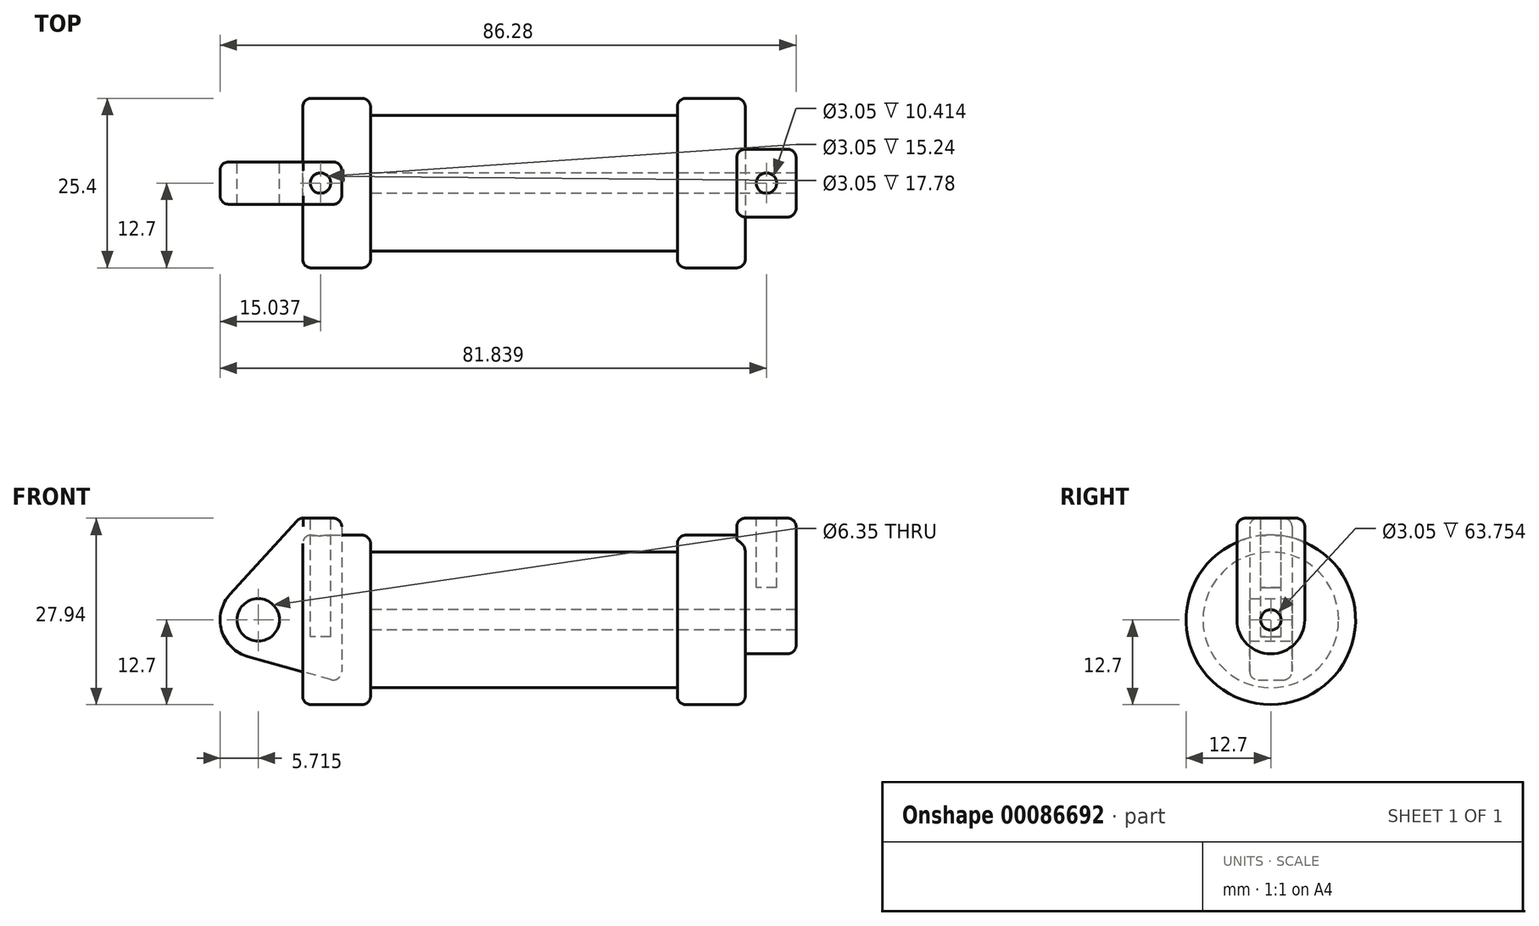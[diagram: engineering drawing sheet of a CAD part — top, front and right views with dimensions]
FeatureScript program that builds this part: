
annotation { "Feature Type Name" : "Feature", "Feature Type Description" : "" }
export const myFeature = defineFeature(function(context is Context, id is Id, definition is map)
    precondition{}
    {
        {
            var Q0;
            Q0=qCreatedBy(makeId("Front.planeOp"),FACE);
            var sketch = newSketch(context, id + "F0", { "sketchPlane" : qUnion([Q0])});
            skLineSegment(sketch, "E0", {"start": v(0, 0) * mm, "end": v(0, 12.7) * mm});
            skLineSegment(sketch, "E1", {"start": v(0, 12.7) * mm, "end": v(10.16, 12.7) * mm});
            skLineSegment(sketch, "E2", {"start": v(10.16, 12.7) * mm, "end": v(10.16, 10.16) * mm});
            skLineSegment(sketch, "E3", {"start": v(10.16, 10.16) * mm, "end": v(56.13, 10.16) * mm});
            skLineSegment(sketch, "E4", {"start": v(56.13, 10.16) * mm, "end": v(56.13, 12.7) * mm});
            skLineSegment(sketch, "E5", {"start": v(56.13, 12.7) * mm, "end": v(66.3, 12.7) * mm});
            skLineSegment(sketch, "E6", {"start": v(66.3, 12.7) * mm, "end": v(66.3, 0) * mm});
            skLineSegment(sketch, "E7", {"start": v(66.3, 0) * mm, "end": v(0, 0) * mm});
            skLineSegment(sketch, "E8", {"start": v(5.84, 15.24) * mm, "end": v(-0.5, 15.24) * mm});
            skLineSegment(sketch, "E9", {"start": v(-0.5, 15.24) * mm, "end": v(-10.88, 3.85) * mm});
            skLineSegment(sketch, "E10", {"start": v(0, 0) * mm, "end": v(-6.65, 0) * mm});
            skCircle(sketch, "E11", {"center": v(-6.65, 0) * mm, "radius": 5.72 * mm});
            skCircle(sketch, "E12", {"center": v(-6.65, 0) * mm, "radius": 3.18 * mm});
            skLineSegment(sketch, "E13", {"start": v(5.84, 15.24) * mm, "end": v(5.84, -9.4) * mm});
            skLineSegment(sketch, "E14", {"start": v(5.84, -9.4) * mm, "end": v(-8.18, -5.5) * mm});
            skSolve(sketch);
        }
        {
            var Q0;
            {var subQ3=sQuery(id+"F0.wireOp",EDGE,"E0");Q0=makeQuery(id+"F0.imprint","IMPRINT",FACE,{"disambiguationData":[TD([[makeQuery(id+"F0.imprint","IMPRINT",EDGE,{"derivedFrom":subQ3}),1.0]])]});}
            var Q1;
            {var subQ4=sQuery(id+"F0.wireOp",EDGE,"E12");Q1=makeQuery(id+"F0.imprint","IMPRINT",FACE,{"disambiguationData":[TD([[makeQuery(id+"F0.imprint","IMPRINT",EDGE,{"derivedFrom":subQ4}),-1.0]])]});}
            var Q2;
            {var subQ0=sQuery(id+"F0.wireOp",EDGE,"E14");Q2=makeQuery(id+"F0.imprint","IMPRINT",FACE,{"disambiguationData":[TD([[makeQuery(id+"F0.imprint","IMPRINT",EDGE,{"derivedFrom":subQ0}),-1.0]])]});}
            var Q3;
            {var subQ0=sQuery(id+"F0.wireOp",EDGE,"E0");Q3=makeQuery(id+"F0.imprint","IMPRINT",FACE,{"disambiguationData":[TD([[makeQuery(id+"F0.imprint","IMPRINT",EDGE,{"derivedFrom":subQ0}),-1.0]])]});}
            extrude(context, id + "F1", {"entities" : qUnion([Q0, Q1, Q2, Q3]), "endBound" : BoundingType.SYMMETRIC, "depth" : 6.35 * mm});
        }
        {
            var Q0;
            {var subQ0=sQuery(id+"F0.wireOp",EDGE,"E2");Q0=makeQuery(id+"F0.imprint","IMPRINT",FACE,{"disambiguationData":[TD([[makeQuery(id+"F0.imprint","IMPRINT",EDGE,{"derivedFrom":subQ0}),-1.0]])]});}
            var Q1;
            {var subQ0=sQuery(id+"F0.wireOp",EDGE,"E0");Q1=makeQuery(id+"F0.imprint","IMPRINT",FACE,{"disambiguationData":[TD([[makeQuery(id+"F0.imprint","IMPRINT",EDGE,{"derivedFrom":subQ0}),-1.0]])]});}
            var Q2;
            Q2=sQuery(id+"F0.wireOp",EDGE,"E7");
            revolve(context, id + "F2", {"entities" : qUnion([Q0, Q1]), "axis" : qUnion([Q2]), "revolveType" : RevolveType.FULL});
        }
        {
            var Q0;
            Q0=makeQuery(id+"F2.opRevolve","SWEPT_FACE",FACE,{"disambiguationData":[OSD([sQuery(id+"F0.wireOp",EDGE,"E6")])]});
            var sketch = newSketch(context, id + "F3", { "sketchPlane" : qUnion([Q0])});
            skCircle(sketch, "E15", {"center": v(0, 0) * mm, "radius": 1.52 * mm});
            skCircle(sketch, "E16", {"center": v(0, 0) * mm, "radius": 5.08 * mm});
            skLineSegment(sketch, "E17", {"start": v(-5.08, 0) * mm, "end": v(-5.08, 15.24) * mm});
            skLineSegment(sketch, "E18", {"start": v(-5.08, 15.24) * mm, "end": v(5.08, 15.24) * mm});
            skLineSegment(sketch, "E19", {"start": v(5.08, 15.24) * mm, "end": v(5.08, 0) * mm});
            skSolve(sketch);
        }
        {
            var Q0;
            {var subQ0=sQuery(id+"F3.wireOp",EDGE,"E18");Q0=makeQuery(id+"F3.imprint","IMPRINT",FACE,{"disambiguationData":[TD([[makeQuery(id+"F3.imprint","IMPRINT",EDGE,{"derivedFrom":subQ0}),-1.0]])]});}
            var Q1;
            {var subQ0=sQuery(id+"F3.wireOp",EDGE,"E17");var subQ1=sQuery(id+"F3.wireOp",EDGE,"E16");var subQ2=makeQuery(id+"F3.imprint","INTERSECT",VERTEX,{"derivedFrom":[subQ1,subQ0]});Q1=makeQuery(id+"F3.imprint","IMPRINT",FACE,{"disambiguationData":[TD([[makeQuery(id+"F3.imprint","IMPRINT",EDGE,{"disambiguationData":[TD([[subQ2,1.0]])],"derivedFrom":subQ1}),-1.0]])]});}
            var Q2;
            Q2=makeQuery(id+"F3.imprint","IMPRINT",FACE,{"disambiguationData":[TD([[makeQuery(id+"F3.imprint","IMPRINT",EDGE,{"derivedFrom":sQuery(id+"F3.wireOp",EDGE,"E15")}),-1.0]])]});
            extrude(context, id + "F4", {"entities" : qUnion([Q0, Q1, Q2]), "operationType" : NewBodyOperationType.ADD, "depth" : 7.62 * mm});
        }
        {
            var Q0;
            {var subQ0=sQuery(id+"F3.wireOp",EDGE,"E18");Q0=makeQuery(id+"F3.imprint","IMPRINT",FACE,{"disambiguationData":[TD([[makeQuery(id+"F3.imprint","IMPRINT",EDGE,{"derivedFrom":subQ0}),-1.0]])]});}
            var Q1;
            {var subQ0=sQuery(id+"F3.wireOp",EDGE,"E17");var subQ1=sQuery(id+"F3.wireOp",EDGE,"E16");var subQ2=makeQuery(id+"F3.imprint","INTERSECT",VERTEX,{"derivedFrom":[subQ1,subQ0]});Q1=makeQuery(id+"F3.imprint","IMPRINT",FACE,{"disambiguationData":[TD([[makeQuery(id+"F3.imprint","IMPRINT",EDGE,{"disambiguationData":[TD([[subQ2,1.0]])],"derivedFrom":subQ1}),-1.0]])]});}
            var Q2;
            Q2=makeQuery(id+"F3.imprint","IMPRINT",FACE,{"disambiguationData":[TD([[makeQuery(id+"F3.imprint","IMPRINT",EDGE,{"derivedFrom":sQuery(id+"F3.wireOp",EDGE,"E15")}),-1.0]])]});
            extrude(context, id + "F5", {"entities" : qUnion([Q0, Q1, Q2]), "operationType" : NewBodyOperationType.ADD, "oppositeDirection" : true, "depth" : 1.27 * mm});
        }
        {
            var Q0;
            Q0=makeQuery(id+"F4.boolean.opBoolean","SPLIT",FACE,{"disambiguationData":[TD([makeQuery(id+"F4.opExtrude","SWEPT_FACE",FACE,{"disambiguationData":[OSD([sQuery(id+"F3.wireOp",EDGE,"E15")])]})])],"derivedFrom":makeQuery(id+"F2.opRevolve","SWEPT_FACE",FACE,{"disambiguationData":[OSD([sQuery(id+"F0.wireOp",EDGE,"E6")])]})});
            var Q1;
            Q1=makeQuery(id+"F2.opRevolve","SWEPT_FACE",FACE,{"disambiguationData":[OSD([sQuery(id+"F0.wireOp",EDGE,"E2")])]});
            extrude(context, id + "F6", {"entities" : qUnion([Q0]), "operationType" : NewBodyOperationType.REMOVE, "endBound" : BoundingType.UP_TO_SURFACE, "oppositeDirection" : true, "endBoundEntityFace" : qUnion([Q1]), "depth" : 25.4 * mm});
        }
        {
            var Q0;
            {var subQ0=sQuery(id+"F3.wireOp",EDGE,"E18");Q0=makeQuery(id+"F5.boolean.opBoolean","MERGE",FACE,{"derivedFrom":[makeQuery(id+"F4.opExtrude","SWEPT_FACE",FACE,{"disambiguationData":[OSD([subQ0])]}),makeQuery(id+"F5.opExtrude","SWEPT_FACE",FACE,{"disambiguationData":[OSD([subQ0])]})]});}
            var sketch = newSketch(context, id + "F7", { "sketchPlane" : qUnion([Q0])});
            skCircle(sketch, "E20", {"center": v(69.47, 0) * mm, "radius": 1.52 * mm});
            skPoint(sketch, "E20.centerSnap0", {"position": v(69.47, 5.08) * mm});
            skPoint(sketch, "E20.centerSnap1", {"position": v(73.91, 0) * mm});
            skSolve(sketch);
        }
        {
            var Q0;
            Q0=makeQuery(id+"F7.imprint","IMPRINT",FACE,{"disambiguationData":[TD([[makeQuery(id+"F7.imprint","IMPRINT",EDGE,{"derivedFrom":sQuery(id+"F7.wireOp",EDGE,"E20")}),1.0]])]});
            extrude(context, id + "F8", {"entities" : qUnion([Q0]), "operationType" : NewBodyOperationType.REMOVE, "oppositeDirection" : true, "depth" : 10.4 * mm});
        }
        {
            var Q0;
            Q0=makeQuery(id+"F1.opExtrude","SWEPT_FACE",FACE,{"disambiguationData":[OSD([sQuery(id+"F0.wireOp",EDGE,"E8")])]});
            var sketch = newSketch(context, id + "F9", { "sketchPlane" : qUnion([Q0])});
            skCircle(sketch, "E21", {"center": v(2.67, 0) * mm, "radius": 1.52 * mm});
            skPoint(sketch, "E21.centerSnap0", {"position": v(2.67, 3.18) * mm});
            skSolve(sketch);
        }
        {
            var Q0;
            Q0=makeQuery(id+"F9.imprint","IMPRINT",FACE,{"disambiguationData":[TD([[makeQuery(id+"F9.imprint","IMPRINT",EDGE,{"derivedFrom":sQuery(id+"F9.wireOp",EDGE,"E21")}),1.0]])]});
            extrude(context, id + "F10", {"entities" : qUnion([Q0]), "operationType" : NewBodyOperationType.REMOVE, "oppositeDirection" : true, "depth" : 17.78 * mm});
        }
        {
            var Q0;
            Q0=makeQuery(id+"F1.opExtrude","CAP_EDGE",EDGE,{"disambiguationData":[OSD([sQuery(id+"F0.wireOp",EDGE,"E8")])],"isStart":true});
            var Q1;
            Q1=makeQuery(id+"F1.opExtrude","SWEPT_EDGE",EDGE,{"disambiguationData":[OSD([sQuery(id+"F0.wireOp",EDGE,"E8"),sQuery(id+"F0.wireOp",EDGE,"E13")])]});
            var Q2;
            Q2=makeQuery(id+"F1.opExtrude","CAP_EDGE",EDGE,{"disambiguationData":[OSD([sQuery(id+"F0.wireOp",EDGE,"E8")])],"isStart":false});
            fillet(context, id + "F11", {"entities" : qUnion([Q0, Q1, Q2]), "radius" : 1.27 * mm, "tangentPropagation" : true, "allowEdgeOverflow" : false});
        }
        {
            var Q0;
            Q0=makeQuery(id+"F2.opRevolve","SWEPT_EDGE",EDGE,{"disambiguationData":[OSD([sQuery(id+"F0.wireOp",EDGE,"E1"),sQuery(id+"F0.wireOp",EDGE,"E2")])]});
            var Q1;
            Q1=makeQuery(id+"F2.opRevolve","SWEPT_EDGE",EDGE,{"disambiguationData":[OSD([sQuery(id+"F0.wireOp",EDGE,"E0"),sQuery(id+"F0.wireOp",EDGE,"E1")])]});
            fillet(context, id + "F12", {"entities" : qUnion([Q0, Q1]), "radius" : 1.27 * mm, "tangentPropagation" : true, "allowEdgeOverflow" : false});
        }
        {
            var Q0;
            Q0=makeQuery(id+"F11.opFillet","BLEND_EDGE",EDGE,{"blendedFrom":[makeQuery(id+"F1.opExtrude","CAP_EDGE",EDGE,{"disambiguationData":[OSD([sQuery(id+"F0.wireOp",EDGE,"E8")])],"isStart":true}),makeQuery(id+"F1.opExtrude","SWEPT_FACE",FACE,{"disambiguationData":[OSD([sQuery(id+"F0.wireOp",EDGE,"E9")])]})],"blendedInto":[makeQuery(id+"F1.opExtrude","SWEPT_FACE",FACE,{"disambiguationData":[OSD([sQuery(id+"F0.wireOp",EDGE,"E9")])]})]});
            var Q1;
            Q1=makeQuery(id+"F1.opExtrude","SWEPT_EDGE",EDGE,{"disambiguationData":[OSD([sQuery(id+"F0.wireOp",EDGE,"E8"),sQuery(id+"F0.wireOp",EDGE,"E9")])]});
            var Q2;
            Q2=makeQuery(id+"F11.opFillet","BLEND_EDGE",EDGE,{"blendedFrom":[makeQuery(id+"F1.opExtrude","CAP_EDGE",EDGE,{"disambiguationData":[OSD([sQuery(id+"F0.wireOp",EDGE,"E8")])],"isStart":false}),makeQuery(id+"F1.opExtrude","SWEPT_FACE",FACE,{"disambiguationData":[OSD([sQuery(id+"F0.wireOp",EDGE,"E9")])]})],"blendedInto":[makeQuery(id+"F1.opExtrude","SWEPT_FACE",FACE,{"disambiguationData":[OSD([sQuery(id+"F0.wireOp",EDGE,"E9")])]})]});
            var Q3;
            Q3=makeQuery(id+"F1.opExtrude","CAP_EDGE",EDGE,{"disambiguationData":[OSD([sQuery(id+"F0.wireOp",EDGE,"E9")])],"isStart":false});
            var Q4;
            Q4=makeQuery(id+"F1.opExtrude","CAP_EDGE",EDGE,{"disambiguationData":[OSD([sQuery(id+"F0.wireOp",EDGE,"E9")])],"isStart":true});
            var Q5;
            Q5=makeQuery(id+"F1.opExtrude","CAP_EDGE",EDGE,{"disambiguationData":[OSD([sQuery(id+"F0.wireOp",EDGE,"E11")])],"isStart":false});
            var Q6;
            Q6=makeQuery(id+"F1.opExtrude","CAP_EDGE",EDGE,{"disambiguationData":[OSD([sQuery(id+"F0.wireOp",EDGE,"E11")])],"isStart":true});
            var Q7;
            Q7=makeQuery(id+"F1.opExtrude","CAP_EDGE",EDGE,{"disambiguationData":[OSD([sQuery(id+"F0.wireOp",EDGE,"E14")])],"isStart":true});
            var Q8;
            Q8=makeQuery(id+"F1.opExtrude","CAP_EDGE",EDGE,{"disambiguationData":[OSD([sQuery(id+"F0.wireOp",EDGE,"E14")])],"isStart":false});
            fillet(context, id + "F13", {"entities" : qUnion([Q0, Q1, Q2, Q3, Q4, Q5, Q6, Q7, Q8]), "radius" : 1.27 * mm, "tangentPropagation" : true, "allowEdgeOverflow" : false});
        }
        {
            var Q0;
            Q0=makeQuery(id+"F1.opExtrude","CAP_EDGE",EDGE,{"disambiguationData":[OSD([sQuery(id+"F0.wireOp",EDGE,"E13")])],"isStart":false});
            var Q1;
            Q1=makeQuery(id+"F1.opExtrude","CAP_EDGE",EDGE,{"disambiguationData":[OSD([sQuery(id+"F0.wireOp",EDGE,"E13")])],"isStart":true});
            fillet(context, id + "F14", {"entities" : qUnion([Q0, Q1]), "radius" : 1.27 * mm, "tangentPropagation" : true, "allowEdgeOverflow" : false});
        }
        {
            var Q0;
            Q0=makeQuery(id+"F4.boolean.opBoolean","SPLIT",EDGE,{"disambiguationData":[OD(1.0)],"derivedFrom":makeQuery(id+"F2.opRevolve","SWEPT_EDGE",EDGE,{"disambiguationData":[OSD([sQuery(id+"F0.wireOp",EDGE,"E5"),sQuery(id+"F0.wireOp",EDGE,"E6")])]})});
            var Q1;
            Q1=makeQuery(id+"F2.opRevolve","SWEPT_EDGE",EDGE,{"disambiguationData":[OSD([sQuery(id+"F0.wireOp",EDGE,"E4"),sQuery(id+"F0.wireOp",EDGE,"E5")])]});
            fillet(context, id + "F15", {"entities" : qUnion([Q0, Q1]), "radius" : 1.27 * mm, "tangentPropagation" : true, "allowEdgeOverflow" : false});
        }
        {
            var Q0;
            Q0=makeQuery(id+"F4.opExtrude","CAP_EDGE",EDGE,{"disambiguationData":[OSD([sQuery(id+"F3.wireOp",EDGE,"E17")])],"isStart":false});
            var Q1;
            Q1=makeQuery(id+"F4.opExtrude","CAP_EDGE",EDGE,{"disambiguationData":[OSD([sQuery(id+"F3.wireOp",EDGE,"E16")])],"isStart":false});
            var Q2;
            Q2=makeQuery(id+"F4.opExtrude","CAP_EDGE",EDGE,{"disambiguationData":[OSD([sQuery(id+"F3.wireOp",EDGE,"E19")])],"isStart":false});
            var Q3;
            Q3=makeQuery(id+"F5.opExtrude","CAP_EDGE",EDGE,{"disambiguationData":[OSD([sQuery(id+"F3.wireOp",EDGE,"E17")])],"isStart":false});
            var Q4;
            {var subQ0=sQuery(id+"F3.wireOp",EDGE,"E18");var subQ1=sQuery(id+"F3.wireOp",EDGE,"E17");Q4=makeQuery(id+"F5.boolean.opBoolean","MERGE",EDGE,{"derivedFrom":[makeQuery(id+"F4.opExtrude","SWEPT_EDGE",EDGE,{"disambiguationData":[OSD([subQ1,subQ0])]}),makeQuery(id+"F5.opExtrude","SWEPT_EDGE",EDGE,{"disambiguationData":[OSD([subQ1,subQ0])]})]});}
            var Q5;
            Q5=makeQuery(id+"F5.opExtrude","CAP_EDGE",EDGE,{"disambiguationData":[OSD([sQuery(id+"F3.wireOp",EDGE,"E18")])],"isStart":false});
            var Q6;
            {var subQ0=sQuery(id+"F3.wireOp",EDGE,"E19");var subQ1=sQuery(id+"F3.wireOp",EDGE,"E18");Q6=makeQuery(id+"F5.boolean.opBoolean","MERGE",EDGE,{"derivedFrom":[makeQuery(id+"F4.opExtrude","SWEPT_EDGE",EDGE,{"disambiguationData":[OSD([subQ1,subQ0])]}),makeQuery(id+"F5.opExtrude","SWEPT_EDGE",EDGE,{"disambiguationData":[OSD([subQ1,subQ0])]})]});}
            var Q7;
            Q7=makeQuery(id+"F4.opExtrude","CAP_EDGE",EDGE,{"disambiguationData":[OSD([sQuery(id+"F3.wireOp",EDGE,"E18")])],"isStart":false});
            var Q8;
            Q8=makeQuery(id+"F5.opExtrude","CAP_EDGE",EDGE,{"disambiguationData":[OSD([sQuery(id+"F3.wireOp",EDGE,"E19")])],"isStart":false});
            fillet(context, id + "F16", {"entities" : qUnion([Q0, Q1, Q2, Q3, Q4, Q5, Q6, Q7, Q8]), "radius" : 1.27 * mm, "tangentPropagation" : true, "allowEdgeOverflow" : false});
        }
    });
